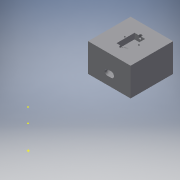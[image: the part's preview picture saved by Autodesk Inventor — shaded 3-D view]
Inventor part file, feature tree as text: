
AUTODESK INVENTOR PART (.ipt)
format: ipt  version: 2016 (Build 200138000, 138)  size: 2,383,872 bytes
history: native  units: mm
features: sketch x64, plane x35, extrude x32, fillet x17, chamfer x4, sweep x2, projected_geometry x2, loft x1, mirror x1, hole x1
ambient origin geometry x8: Origin, YZ Plane, XZ Plane, XY Plane, X Axis, Y Axis, Z Axis, Center Point
bodies: Body1 (feature_tree)
feature tree (159):
  sketch  "Sketch1"  dims[d1=8.0mm d2=7.0mm]
  plane  "Work Plane4"
  sketch  "Sketch2"  dims[d3=7.0mm d4=8.0mm d8=20.0mm d9=-3.490659mm d11=8.0mm d12=8.0mm d14=2.0mm d15=10.0mm d17=-1.745329mm d18=1.0mm d19=11.75mm]
  sketch  "Sketch3"  dims[d20=20.0mm d21=9.5mm]
  sketch  "Sketch4"  dims[d22=8.0mm d23=0.0mm d25=9.0mm]
  sketch  "Sketch5"  dims[d27=8.5mm d28=3.0mm]
  sketch  "Sketch6"  dims[d29=-1.745329mm d30=-3.490659mm d31=1.0mm d32=2.0mm d33=8.6mm]
  plane  "Work Plane5"
  sketch  "Sketch7"  dims[d34=8.5mm d35=7.0mm]
  plane  "Work Plane7"
  sketch  "Sketch8"  dims[d36=7.0mm d37=5.0mm d38=3.0mm]
  plane  "Work Plane8"
  sketch  "Sketch9"  dims[d39=17.0mm]
  plane  "Work Plane10"
  sketch  "Sketch10"  dims[d40=8.0mm]
  plane  "Work Plane11"
  plane  "Work Plane12"
  sketch  "Sketch11"  dims[d41=17.0mm]
  sketch  "Sketch12"  dims[d42=7.7mm]
  sketch  "Sketch13"  dims[d43=17.0mm]
  plane  "Work Plane13"
  plane  "Work Plane14"
  plane  "Work Plane15"
  plane  "Work Plane16"
  sketch  "Sketch14"  dims[d44=6.8mm]
  sketch  "Sketch15"  dims[d45=17.0mm]
  plane  "Work Plane20"
  sketch  "Sketch16"  dims[d46=5.0mm]
  sketch  "Sketch17"  dims[d47=2.0mm]
  sketch  "Sketch18"  dims[d48=17.0mm]
  sketch  "Sketch19"  dims[d49=2.0mm]
  plane  "Work Plane21"
  loft  "Loft1"
  extrude  "Extrusion1"  Depth=10.0mm
  fillet  "Fillet1"  [1 undecoded]
  fillet  "Fillet2"  Radius=8.0mm
  fillet  "Fillet3"  Radius=2.0mm
  fillet  "Fillet4"  Radius=10.0mm
  fillet  "Fillet5"  Radius=1.0mm
  fillet  "Fillet6"  Radius=11.75mm
  plane  "Work Plane23"
  plane  "Work Plane25"
  sketch  "Sketch22"  dims[d75=0.0mm d76=90.0deg d77=0.0mm d78=90.0deg d79=0.0mm d80=90.0deg]
  extrude  "Extrusion2"  Depth=9.5mm
  plane  "Work Plane26"
  sketch  "Sketch24"  dims[d85=0.3mm d86=6.0mm]
  sketch  "Sketch25"  dims[d87=6.0mm d88=2.0mm]
  extrude  "Extrusion3"  Depth=9.0mm
  extrude  "Extrusion4"  Depth=3.0mm
  sketch  "Sketch27"  dims[d90=2.0mm]
  extrude  "Extrusion5"  Depth=8.6mm
  sketch  "Sketch29"  dims[d96=2.0mm d97=2.0mm]
  extrude  "Extrusion6"  Depth=7.0mm
  extrude  "Extrusion7"  Depth=5.0mm
  mirror  "Mirror1"
  chamfer  "Chamfer1"  Angle=90.0deg  [1 undecoded]
  fillet  "Fillet7"  [1 undecoded]
  fillet  "Fillet8"  [1 undecoded]
  fillet  "Fillet9"  [1 undecoded]
  fillet  "Fillet10"  [1 undecoded]
  chamfer  "Chamfer2"  Angle=90.0deg  [1 undecoded]
  fillet  "Fillet12"  [1 undecoded]
  fillet  "Fillet13"  [1 undecoded]
  fillet  "Fillet14"  [1 undecoded]
  fillet  "Fillet17"  [1 undecoded]
  sketch  "Sketch31"  dims[d100=90.0deg d101=22.0mm d102=12.217305mm d103=20.0mm d110=3.0mm]
  plane  "Work Plane27"
  extrude  "Extrusion9"  TaperAngle=0.0deg  [1 undecoded]
  extrude  "Extrusion10"  TaperAngle=0.0deg  [1 undecoded]
  chamfer  "Chamfer4"  Angle=90.0deg  [1 undecoded]
  extrude  "Extrusion11"  TaperAngle=0.0deg  [1 undecoded]
  extrude  "Extrusion12"  Depth=6.0mm
  extrude  "Extrusion13"  Depth=2.0mm
  chamfer  "Chamfer5"  Distance=15.0mm
  plane  "Work Plane28"
  fillet  "Fillet19"  Radius=2.0mm
  fillet  "Fillet20"  Radius=2.0mm
  plane  "Work Plane37"
  extrude  "Extrusion25"  Depth=2.0mm
  extrude  "Extrusion27"  Depth=2.0mm
  extrude  "Extrusion28"  Depth=12.217305mm
  plane  "Work Plane38"
  sketch  "Sketch63"  dims[d136=2.0mm d137=12.0mm]
  sketch  "Sketch47"  dims[d126=12.0mm d127=6.0mm]
  fillet  "Fillet21"  Radius=3.0mm
  plane  "Work Plane39"
  plane  "Work Plane40"
  plane  "Work Plane42"
  extrude  "Extrusion35"  Depth=8.0mm
  sweep  "Sweep6"
  sketch  "Sketch79"  dims[d160=0.5mm d161=1.0mm]
  plane  "Work Plane44"
  extrude  "Extrusion37"  Depth=20.0mm
  extrude  "Extrusion38"  Depth=10.0mm
  extrude  "Extrusion39"  Depth=4.0mm
  sketch  "Sketch84"  dims[d178=2.8mm d179=0.0mm]
  extrude  "Extrusion40"  Depth=6.0mm
  extrude  "Extrusion41"  Depth=10.75mm
  extrude  "Extrusion42"  Depth=9.0mm
  extrude  "Extrusion43"  Depth=30.0mm
  extrude  "Extrusion44"  Depth=12.0mm
  extrude  "Extrusion45"  Depth=1.2mm
  extrude  "Extrusion46"  Depth=8.0mm
  extrude  "Extrusion47"  Depth=12.0mm TaperAngle=0.0deg
  hole  "Hole1"  [1 undecoded]
  extrude  "Extrusion48"  Depth=0.5mm
  extrude  "Extrusion49"  Depth=1.0mm
  extrude  "Extrusion32"  Depth=1.0mm
  extrude  "Extrusion33"  Depth=1.0mm
  sketch  "Sketch71"  dims[d143=1.2mm d144=12.0mm d145=0.0mm]
  sketch  "Sketch72"  dims[d146=20.0mm d147=0.0mm d148=0.5mm d149=2.0mm d150=45.0deg]
  sweep  "Sweep8"
  sketch  "Sketch74"  dims[d151=1.0mm d152=0.5mm]
  plane  "Work Plane43"
  extrude  "Extrusion36"  Depth=2.7mm TaperAngle=0.0deg
  plane  "Work Plane1"
  plane  "Work Plane2"
  plane  "Work Plane3"
  plane  "Work Plane6"
  plane  "Work Plane9"
  plane  "Work Plane17"
  plane  "Work Plane18"
  plane  "Work Plane19"
  sketch  "Sketch20"  dims[d50=2.0mm d51=0.0mm d52=90.0deg d53=0.0mm d54=90.0deg d55=0.0mm d56=90.0deg d57=0.0mm d58=90.0deg d59=0.0mm d60=90.0deg d61=0.0mm d62=90.0deg d63=0.0mm d64=90.0deg d65=0.0mm d66=90.0deg d67=0.0mm d68=90.0deg d69=0.0mm d70=90.0deg]
  sketch  "Sketch21"  dims[d71=0.0mm d72=90.0deg d73=0.0mm d74=90.0deg]
  plane  "Work Plane22"
  plane  "Work Plane24"
  sketch  "Sketch23"  dims[d81=0.0mm d82=90.0deg d83=0.0mm d84=90.0deg]
  sketch  "Sketch26"  dims[d89=135.0deg]
  sketch  "Sketch28"  dims[d91=45.0deg d92=15.0mm d93=0.0mm d94=2.0mm d95=2.0mm]
  sketch  "Sketch30"  dims[d98=2.0mm d99=2.0mm]
  sketch  "Sketch32"  dims[d111=6.0mm d112=8.0mm]
  sketch  "Sketch33"  dims[d113=6.0mm d114=20.0mm d115=0.0mm]
  sketch  "Sketch34"  dims[d116=12.0mm d117=20.0mm]
  sketch  "Sketch35"  dims[d118=10.0mm d123=2.0mm]
  sketch  "Sketch36"  dims[d124=4.0mm d125=4.0mm]
  sketch  "Sketch58"  dims[d128=6.0mm d129=0.0mm d130=10.75mm]
  sketch  "Sketch59"  dims[d131=9.0mm d132=9.0mm]
  sketch  "Sketch60"  dims[d133=60.0mm d134=0.0mm d135=30.0mm]
  sketch  "Sketch68"  dims[d138=6.0mm d139=0.0mm d140=1.2mm]
  sketch  "Sketch70"  dims[d141=8.0mm d142=8.0mm]
  projected_geometry  "Projected Loop1"
  sketch  "Sketch76"  dims[d153=0.5mm d154=1.0mm]
  sketch  "Sketch77"  dims[d156=0.5mm d157=2.0mm d158=45.0deg d159=1.0mm]
  projected_geometry  "Projected Loop2"
  sketch  "Sketch80"  dims[d164=0.5mm d167=4.2mm d168=0.0mm]
  sketch  "Sketch81"  dims[d172=4.5mm d173=2.7mm d174=0.0mm]
  sketch  "Sketch83"  dims[d175=2.0mm d176=2.0mm d177=45.0deg]
  sketch  "Sketch85"  dims[d180=14.0mm]
  sketch  "Sketch86"  dims[d181=4.2mm d182=0.0mm]
  sketch  "Sketch87"  dims[d183=2.8mm d184=0.0mm]
  sketch  "Sketch88"  dims[d185=2.0mm d186=2.0mm d187=45.0deg]
  sketch  "Sketch89"  dims[d188=60.0deg]
  sketch  "Sketch90"  dims[d262=3.85mm]
  sketch  "Sketch91"  dims[d263=1.0mm]
  sketch  "Sketch92"  dims[d264=0.25mm]
  sketch  "Sketch93"  dims[d265=-31.0mm]
  sketch  "Sketch94"  dims[d272=72.0mm]
  sketch  "Sketch95"  dims[d273=24.0mm d274=16.0mm d275=10.0mm d276=0.0mm d277=72.5mm d278=12.7mm d279=7.5mm d280=0.5mm d281=2.0mm d282=0.5mm d283=2.0mm d284=72.5mm d286=1.5mm d287=1.0mm d288=1.5mm d289=1.0mm d292=4.0mm d293=0.0mm d294=2.0mm d295=0.5mm d296=2.0mm d297=0.0mm d303=2.5mm d304=5.5mm d305=2.25mm d313=0.25mm d315=-2.1mm d316=52.0mm d317=10.2mm d318=7.5mm d321=2.0mm d322=0.5mm d323=0.5mm d324=2.0mm d325=1.0mm d326=1.5mm d327=1.0mm d328=1.5mm d329=4.0mm d330=0.0mm d335=2.0mm d337=2.0mm d338=0.0mm d339=57.6mm d340=3.0mm d341=3.0mm d342=2.0mm d345=26.598818mm d346=2.939134mm d347=3.263766mm d348=35.5mm d349=6.9mm d350=16.0mm d351=36.8mm d352=5.394mm d358=0.0mm d359=0.0mm d362=0.0mm d363=0.0mm d368=4.5mm d369=1.5mm d370=0.0mm d371=2.0mm d374=1.5mm d375=0.0mm d376=-10.0mm d377=15.0mm d378=30.0mm d379=20.0mm d380=30.0mm d381=30.0mm d382=30.0mm d383=10.0mm d384=0.0mm d385=17.7mm d386=10.0mm d387=0.0mm d388=60.0mm d389=0.0mm d390=2.5mm d391=30.0mm d392=8.5mm d393=30.0mm d394=15.0mm d395=5.0mm d396=10.0mm d397=26.0mm d398=0.0mm d399=6.0mm d400=30.0mm d401=0.0mm d402=10.0mm d403=30.0mm d404=0.0mm d405=30.0mm d406=0.0mm d407=11.0mm d408=4.0mm d409=11.0mm d410=4.0mm d411=30.0mm d412=0.0mm d413=15.0mm d414=0.0mm d415=2.0mm d416=2.0mm d417=11.5mm d418=2.0mm d419=11.5mm d420=15.0mm d421=0.0mm d422=8.5mm d423=0.0mm d424=5.85mm d425=1.0mm d426=10.0mm d427=1.0mm d428=6.0mm d429=4.0mm d430=2.0mm d431=90.0deg d432=4.0mm d433=0.0mm d434=1.5mm d435=0.0mm d436=5.706mm d437=1.25mm d438=2.5mm d439=2.005mm d440=1.25mm d441=2.005mm d442=2.5mm d443=1.5mm d444=0.0mm]
note: 16 required parameter values undecoded (feature->parameter linkage not recoverable at this tier; creation-order binding heuristic only, values carry confidence <= 0.55)
